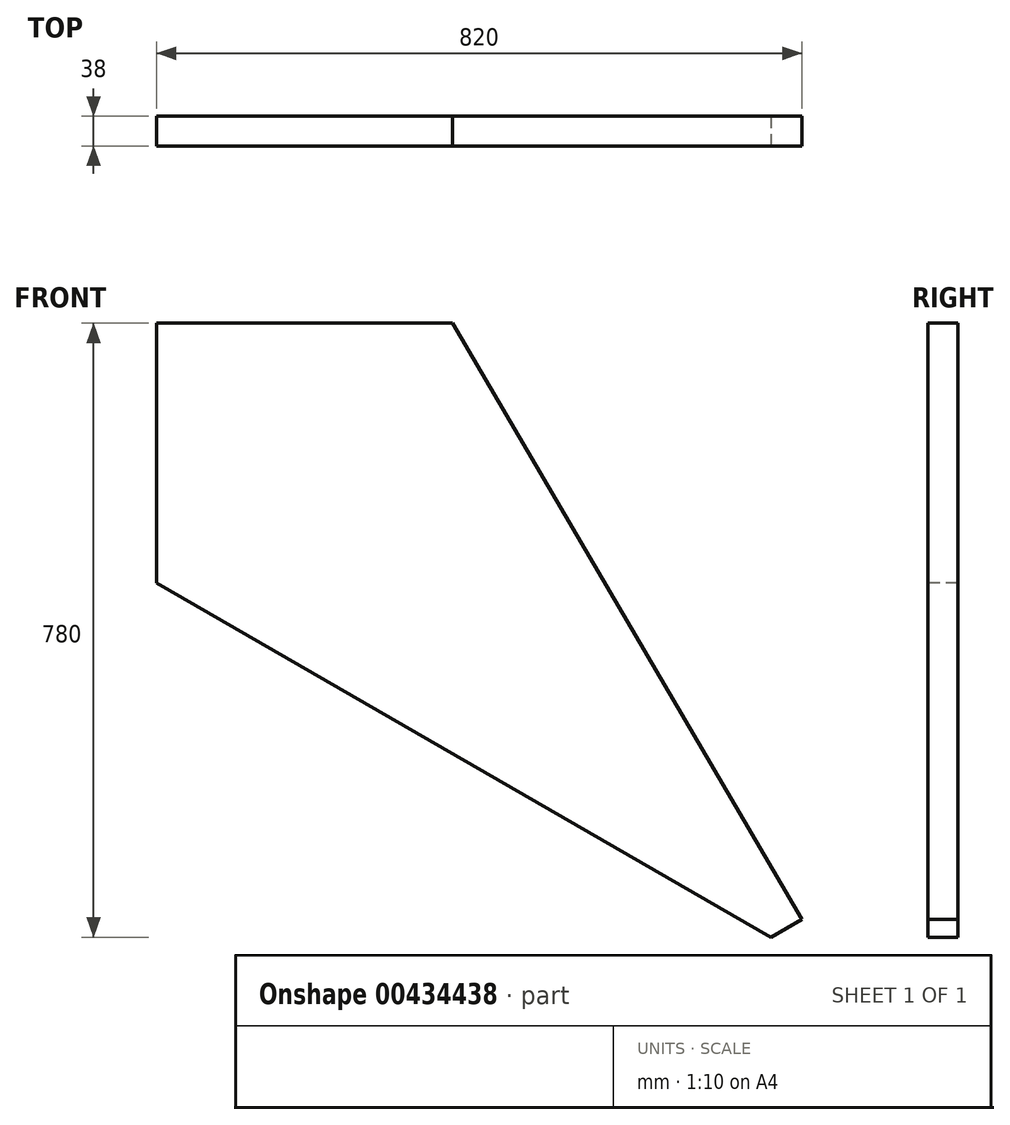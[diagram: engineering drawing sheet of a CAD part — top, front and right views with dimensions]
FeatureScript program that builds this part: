
annotation { "Feature Type Name" : "Feature", "Feature Type Description" : "" }
export const myFeature = defineFeature(function(context is Context, id is Id, definition is map)
    precondition{}
    {
        {
            var Q0;
            Q0=qCreatedBy(makeId("Front.planeOp"),FACE);
            var sketch = newSketch(context, id + "F0", { "sketchPlane" : qUnion([Q0])});
            skLineSegment(sketch, "E0.bottom", {"start": v(-410, 390) * mm, "end": v(410, 390) * mm});
            skLineSegment(sketch, "E0.top", {"start": v(-410, -390) * mm, "end": v(410, -390) * mm});
            skLineSegment(sketch, "E0.left", {"start": v(-410, 390) * mm, "end": v(-410, -390) * mm});
            skLineSegment(sketch, "E0.right", {"start": v(410, 390) * mm, "end": v(410, -390) * mm});
            skLineSegment(sketch, "E1", {"start": v(-410, 390) * mm, "end": v(410, -390) * mm, "construction": true});
            skSolve(sketch);
        }
        {
            var Q0;
            Q0=qSketchRegion(id+"F0",true);
            extrude(context, id + "F1", {"entities" : qUnion([Q0]), "endBound" : BoundingType.SYMMETRIC, "depth" : 38 * mm, "offsetDistance" : 25 * mm});
        }
        {
            var Q0;
            Q0=makeQuery(id+"F1.opExtrude","CAP_FACE",FACE,{"disambiguationData":[OSD([sQuery(id+"F0.wireOp",EDGE,"E0.bottom"),sQuery(id+"F0.wireOp",EDGE,"E0.top"),sQuery(id+"F0.wireOp",EDGE,"E0.left"),sQuery(id+"F0.wireOp",EDGE,"E0.right")])],"isStart":false});
            var sketch = newSketch(context, id + "F2", { "sketchPlane" : qUnion([Q0])});
            skLineSegment(sketch, "E2", {"start": v(-410, 60) * mm, "end": v(370.58, -390) * mm});
            skLineSegment(sketch, "E3", {"start": v(370.58, -390) * mm, "end": v(-410, -390) * mm});
            skLineSegment(sketch, "E4", {"start": v(-410, -390) * mm, "end": v(-410, 60) * mm});
            skLineSegment(sketch, "E5", {"start": v(410, -367.46) * mm, "end": v(-34, 390) * mm});
            skLineSegment(sketch, "E6", {"start": v(-34, 390) * mm, "end": v(410, 390) * mm});
            skLineSegment(sketch, "E7", {"start": v(410, 390) * mm, "end": v(410, -367.46) * mm});
            skLineSegment(sketch, "E8", {"start": v(370.58, -390) * mm, "end": v(410, -367.46) * mm});
            skSolve(sketch);
        }
        {
            var Q0;
            Q0=qSketchRegion(id+"F2",true);
            var Q1;
            {var subQ0=sQuery(id+"F2.wireOp",EDGE,"E8");Q1=makeQuery(id+"F2.imprint","IMPRINT",FACE,{"disambiguationData":[TD([[makeQuery(id+"F2.imprint","IMPRINT",EDGE,{"derivedFrom":subQ0}),-1.0]])]});}
            extrude(context, id + "F3", {"entities" : qUnion([Q0, Q1]), "operationType" : NewBodyOperationType.REMOVE, "endBound" : BoundingType.THROUGH_ALL, "oppositeDirection" : true, "depth" : 25 * mm});
        }
    });
